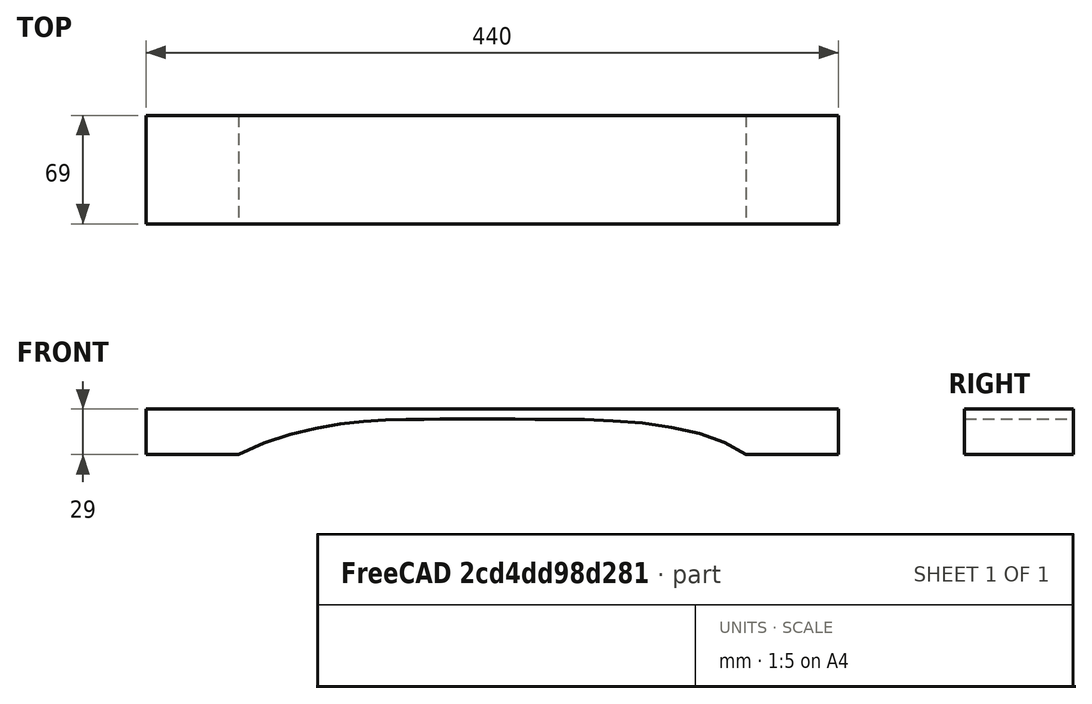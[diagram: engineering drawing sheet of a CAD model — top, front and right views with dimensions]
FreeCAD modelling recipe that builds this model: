
FCSTD DOCUMENT  (FreeCAD 0.20R29410 (Git))
Label: Single_Bar3
License: All rights reserved
LicenseURL: http://en.wikipedia.org/wiki/All_rights_reserved
objects: Sketcher::SketchObject×1, Part::Extrusion×1, Fem::FemSolverObjectPython×1, App::MaterialObjectPython×1, Fem::ConstraintDisplacement×1, Fem::FemMeshShapeNetgenObject×1, Fem::FemAnalysis×1
note: 2 computed .brp shape members not serialized (recipe doc carries the construction recipe); baked Part::Feature solids carry a one-line shape summary decoded from their .brp

FEATURE [Sketcher::SketchObject] Sketch
  FullyConstrained = true
  Placement = pos=(0,0,0) rot=(1,0,0;1.5708rad)
  sketch-geometry (12):
    g0: LineSegment StartX=58.89 StartY=0 StartZ=0 EndX=0 EndY=0 EndZ=0
    g1: LineSegment StartX=0 StartY=0 StartZ=0 EndX=0 EndY=29 EndZ=0
    g2: LineSegment StartX=0 StartY=29 StartZ=0 EndX=440 EndY=29 EndZ=0
    g3: LineSegment StartX=440 StartY=29 StartZ=0 EndX=440 EndY=0 EndZ=0
    g4: LineSegment StartX=440 StartY=0 StartZ=0 EndX=381.11 EndY=0 EndZ=0
    g5-g10: Circle x6 (B-spline internal-alignment scaffolding for g11; pole/knot coordinates omitted)
    g11: BSplineCurve PolesCount=6 KnotsCount=4 Degree=3 IsPeriodic=0
  constraints (38):
    c: DistanceX(g0) = 0
    c: DistanceY(g0) = 0
    c: Distance(g1,g1) = 29
    c: Distance(g2,g2) = 440
    c: DistanceX(g0,g0) = 58.89
    c: DistanceX(g4,g4) = 58.89
    c: Horizontal(g0)
    c: Vertical(g1)
    c: Horizontal(g2)
    c: Vertical(g3)
    c: Horizontal(g4)
    c: Equal(g3,g1)
    c: Coincident(g0,g1)
    c: Coincident(g1,g2)
    c: Coincident(g2,g3)
    c: Coincident(g3,g4)
    c: DistanceX(g6) = 349.72
    c: DistanceY(g6) = 22.44
    c: DistanceX(g7) = 227.77
    c: DistanceY(g7) = 22.31
    c: DistanceX(g8) = 188.46
    c: DistanceY(g8) = 22.98
    c: DistanceX(g9) = 100.31
    c: DistanceY(g9) = 21.1
    c: Weight(g5) = 1
    c: InternalAlignment(g5,g11)
    c: Weight(g6) = 1
    c: InternalAlignment(g6,g11)
    c: Weight(g7) = 1
    c: InternalAlignment(g7,g11)
    c: Weight(g8) = 1
    c: InternalAlignment(g8,g11)
    c: Weight(g9) = 1
    c: InternalAlignment(g9,g11)
    c: Weight(g10) = 1
    c: InternalAlignment(g10,g11)
    c: Coincident(g4,g11)
    c: Coincident(g0,g11)
FEATURE [Part::Extrusion] Bar
  Base = -> Sketch
  Dir = (0,-1,-3e-16)
  DirMode = 2
  FaceMakerClass = Part::FaceMakerBullseye
  LengthFwd = 69
  LengthRev = 0
  Solid = true
  Symmetric = false
FEATURE [Fem::FemSolverObjectPython] SolverCcxTools  # FEM object (typed FeaturePython)
  AnalysisType = 0
  BeamShellResultOutput3D = false
  BucklingFactors = 1
  EigenmodeHighLimit = 20000
  EigenmodeLowLimit = 20
  EigenmodesCount = 12
  GeometricalNonlinearity = 0
  IterationsControlParameterCutb = 0.25,0.5,0.75,0.85,,,1.5,
  IterationsControlParameterIter = 4,8,9,200,10,400,,200,,
  IterationsControlParameterTimeUse = false
  IterationsThermoMechMaximum = 2000
  IterationsUserDefinedIncrementations = false
  IterationsUserDefinedTimeStepLength = false
  MaterialNonlinearity = 0
  MatrixSolverType = 0
  SplitInputWriter = false
  ThermoMechSteadyState = false
  TimeEnd = 1
  TimeInitialStep = 0.01
FEATURE [App::MaterialObjectPython] MaterialSolid  # material (typed FeaturePython)
  Category = 0
  Material = CompressiveStrength=4800 kPa; Density=500 kg/m^3; Name=Wood-Cherry; PoissonRatio=0.39; ShearModulus=11.7 MPa; UltimateTensileStrength=85.0 MPa; YoungsModulus=10300 MPa
FEATURE [Fem::ConstraintDisplacement] FemConstraintDisplacement
  NormalDirection = (0,3e-16,-1)
  Normals = (116) [(0,3.33067e-16,-1),(0,3.33067e-16,-1),(0,3.33067e-16,-1),(0,3.33067e-16,-1),(0,3.33067e-16,-1),(0,3.33067e-16,-1),(0,3.33067e-16,-1),+109 more]
  Points = (116) [(58.89,-69,-2.29816e-14),(39.26,-69,-2.29816e-14),(19.63,-69,-2.29816e-14),(0,-69,-2.29816e-14),(58.89,-46,-1.53211e-14),(39.26,-46,-1.53211e-14),+110 more]
  References = -> [Bar]
  rotxFix = false
  rotxFree = true
  rotyFix = false
  rotyFree = true
  rotzFix = false
  rotzFree = true
  xDisplacement = 0
  xFix = false
  xFree = true
  xRotation = 0
  yDisplacement = 0
  yFix = true
  yFree = false
  yRotation = 0
  zDisplacement = 0
  zFix = false
  zFree = true
  zRotation = 0
FEATURE [Fem::FemMeshShapeNetgenObject] FEMMeshNetgen
  Fineness = 4
  GrowthRate = 0.3
  MaxSize = 10
  NbSegsPerEdge = 1
  NbSegsPerRadius = 2
  Optimize = true
  SecondOrder = true
  Shape = -> Bar
FEATURE [Fem::FemAnalysis] Analysis
  Group = -> [SolverCcxTools,MaterialSolid,FemConstraintDisplacement,FEMMeshNetgen]
